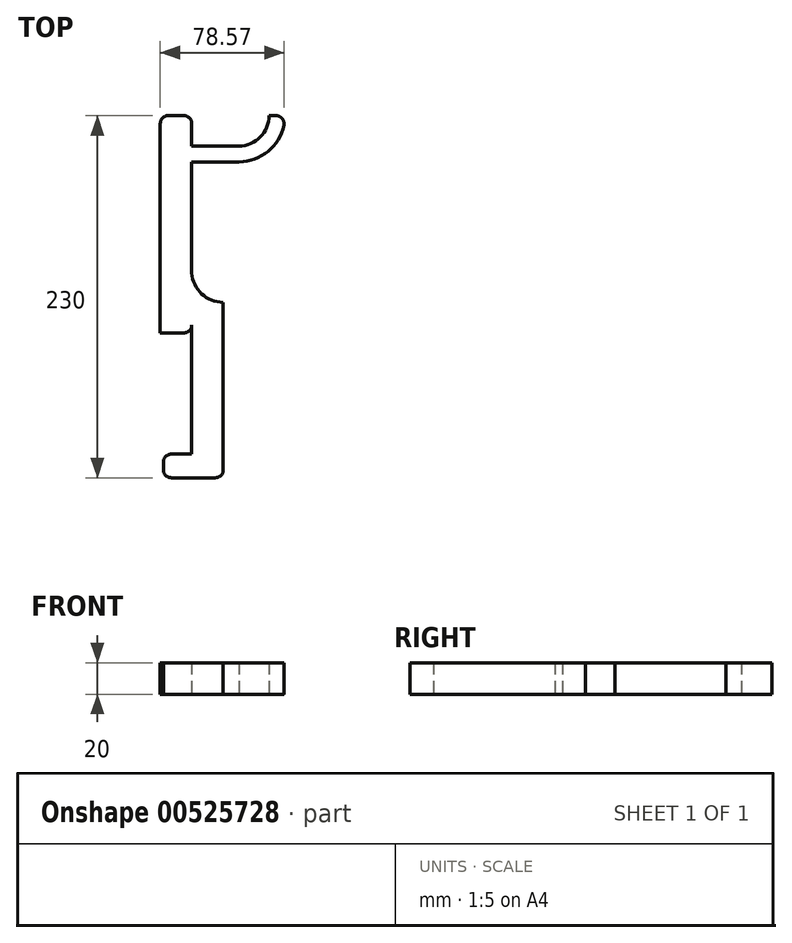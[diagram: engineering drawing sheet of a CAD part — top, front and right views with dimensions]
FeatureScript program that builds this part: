
annotation { "Feature Type Name" : "Feature", "Feature Type Description" : "" }
export const myFeature = defineFeature(function(context is Context, id is Id, definition is map)
    precondition{}
    {
        {
            var Q0;
            Q0=qCreatedBy(makeId("Top.planeOp"),FACE);
            var sketch = newSketch(context, id + "F0", { "sketchPlane" : qUnion([Q0])});
            skLineSegment(sketch, "E0.bottom", {"start": v(-121.25, 37.3) * mm, "end": v(-108.25, 37.3) * mm});
            skLineSegment(sketch, "E0.top", {"start": v(-121.25, 22.3) * mm, "end": v(-108.25, 22.3) * mm});
            skLineSegment(sketch, "E0.left", {"start": v(-126.25, 32.3) * mm, "end": v(-126.25, 27.3) * mm});
            skLineSegment(sketch, "E0.right", {"start": v(-108.25, 37.3) * mm, "end": v(-108.25, 22.3) * mm});
            skLineSegment(sketch, "E1.bottom", {"start": v(-108.25, 22.3) * mm, "end": v(-93.25, 22.3) * mm});
            skLineSegment(sketch, "E1.top", {"start": v(-108.25, 129.3) * mm, "end": v(-88.25, 129.3) * mm});
            skLineSegment(sketch, "E1.left", {"start": v(-108.25, 22.3) * mm, "end": v(-108.25, 129.3) * mm});
            skLineSegment(sketch, "E1.right", {"start": v(-88.25, 27.3) * mm, "end": v(-88.25, 129.3) * mm});
            skLineSegment(sketch, "E2.bottom", {"start": v(-108.25, 129.3) * mm, "end": v(-128.25, 129.3) * mm});
            skLineSegment(sketch, "E2.top", {"start": v(-113.25, 114.3) * mm, "end": v(-128.25, 114.3) * mm});
            skLineSegment(sketch, "E2.left", {"start": v(-108.25, 129.3) * mm, "end": v(-108.25, 119.3) * mm});
            skLineSegment(sketch, "E2.right", {"start": v(-128.25, 129.3) * mm, "end": v(-128.25, 114.3) * mm});
            skLineSegment(sketch, "E3.top", {"start": v(-113.25, 252.3) * mm, "end": v(-123.25, 252.3) * mm});
            skLineSegment(sketch, "E3.left", {"start": v(-108.25, 129.3) * mm, "end": v(-108.25, 247.3) * mm});
            skLineSegment(sketch, "E3.right", {"start": v(-128.25, 129.3) * mm, "end": v(-128.25, 247.3) * mm});
            skArc(sketch, "E4", {"start": v(-108.25, 152.46) * mm, "mid": v(-101.95, 139.16) * mm, "end": v(-88.25, 133.75) * mm});
            skLineSegment(sketch, "E5", {"start": v(-88.25, 129.3) * mm, "end": v(-88.25, 133.75) * mm});
            skPoint(sketch, "E6.visualSharp", {"position": v(-88.25, 22.3) * mm});
            skArc(sketch, "E6.filletArc", {"start": v(-93.25, 22.3) * mm, "mid": v(-89.72, 23.77) * mm, "end": v(-88.25, 27.3) * mm});
            skPoint(sketch, "E7.visualSharp", {"position": v(-126.25, 22.3) * mm});
            skArc(sketch, "E7.filletArc", {"start": v(-126.25, 27.3) * mm, "mid": v(-124.8, 23.77) * mm, "end": v(-121.25, 22.3) * mm});
            skPoint(sketch, "E8.visualSharp", {"position": v(-126.25, 37.3) * mm});
            skArc(sketch, "E8.filletArc", {"start": v(-121.25, 37.3) * mm, "mid": v(-124.8, 35.84) * mm, "end": v(-126.25, 32.3) * mm});
            skPoint(sketch, "E9.visualSharp", {"position": v(-128.25, 252.3) * mm});
            skArc(sketch, "E9.filletArc", {"start": v(-123.25, 252.3) * mm, "mid": v(-126.8, 250.84) * mm, "end": v(-128.25, 247.3) * mm});
            skLineSegment(sketch, "E10.bottom", {"start": v(-108.25, 232.98) * mm, "end": v(-78.25, 232.98) * mm});
            skLineSegment(sketch, "E10.top", {"start": v(-108.25, 222.98) * mm, "end": v(-78.25, 222.98) * mm});
            skLineSegment(sketch, "E10.left", {"start": v(-108.25, 232.98) * mm, "end": v(-108.25, 222.98) * mm});
            skLineSegment(sketch, "E10.right", {"start": v(-78.25, 232.98) * mm, "end": v(-78.25, 222.98) * mm});
            skArc(sketch, "E11", {"start": v(-78.25, 222.98) * mm, "mid": v(-59.91, 229.6) * mm, "end": v(-49.78, 246.28) * mm});
            skArc(sketch, "E12", {"start": v(-78.25, 232.98) * mm, "mid": v(-64.74, 238.72) * mm, "end": v(-59.16, 252.3) * mm});
            skLineSegment(sketch, "E13", {"start": v(-59.16, 252.3) * mm, "end": v(-54.68, 252.3) * mm});
            skPoint(sketch, "E14.visualSharp", {"position": v(-49.16, 252.3) * mm});
            skArc(sketch, "E14.filletArc", {"start": v(-49.78, 246.28) * mm, "mid": v(-50.8, 250.46) * mm, "end": v(-54.68, 252.3) * mm});
            skPoint(sketch, "E15.visualSharp", {"position": v(-108.25, 252.3) * mm});
            skArc(sketch, "E15.filletArc", {"start": v(-108.25, 247.3) * mm, "mid": v(-109.72, 250.84) * mm, "end": v(-113.25, 252.3) * mm});
            skPoint(sketch, "E16.visualSharp", {"position": v(-108.25, 114.3) * mm});
            skArc(sketch, "E16.filletArc", {"start": v(-113.25, 114.3) * mm, "mid": v(-109.72, 115.77) * mm, "end": v(-108.25, 119.3) * mm});
            skSolve(sketch);
        }
        {
            var Q0;
            {var subQ2=sQuery(id+"F0.wireOp",EDGE,"E0.bottom");Q0=makeQuery(id+"F0.imprint","IMPRINT",FACE,{"disambiguationData":[TD([[makeQuery(id+"F0.imprint","IMPRINT",EDGE,{"derivedFrom":subQ2}),-1.0]])]});}
            var Q1;
            Q1=makeQuery(id+"F0.imprint","IMPRINT",FACE,{"disambiguationData":[TD([[makeQuery(id+"F0.imprint","IMPRINT",EDGE,{"derivedFrom":sQuery(id+"F0.wireOp",EDGE,"E10.right")}),1.0]])]});
            var Q2;
            {var subQ0=sQuery(id+"F0.wireOp",EDGE,"E1.top");Q2=makeQuery(id+"F0.imprint","IMPRINT",FACE,{"disambiguationData":[TD([[makeQuery(id+"F0.imprint","IMPRINT",EDGE,{"derivedFrom":subQ0}),1.0]])]});}
            var Q3;
            Q3=makeQuery(id+"F0.imprint","IMPRINT",FACE,{"disambiguationData":[TD([[makeQuery(id+"F0.imprint","IMPRINT",EDGE,{"derivedFrom":sQuery(id+"F0.wireOp",EDGE,"E2.top")}),-1.0]])]});
            var Q4;
            Q4=makeQuery(id+"F0.imprint","IMPRINT",FACE,{"disambiguationData":[TD([[makeQuery(id+"F0.imprint","IMPRINT",EDGE,{"derivedFrom":sQuery(id+"F0.wireOp",EDGE,"E10.bottom")}),-1.0]])]});
            var Q5;
            {var subQ3=sQuery(id+"F0.wireOp",EDGE,"E1.bottom");Q5=makeQuery(id+"F0.imprint","IMPRINT",FACE,{"disambiguationData":[TD([[makeQuery(id+"F0.imprint","IMPRINT",EDGE,{"derivedFrom":subQ3}),1.0]])]});}
            var Q6;
            {var subQ3=sQuery(id+"F0.wireOp",EDGE,"E2.bottom");Q6=makeQuery(id+"F0.imprint","IMPRINT",FACE,{"disambiguationData":[TD([[makeQuery(id+"F0.imprint","IMPRINT",EDGE,{"derivedFrom":subQ3}),-1.0]])]});}
            extrude(context, id + "F1", {"entities" : qUnion([Q0, Q1, Q2, Q3, Q4, Q5, Q6]), "depth" : 20 * mm, "offsetDistance" : 25 * mm});
        }
    });
